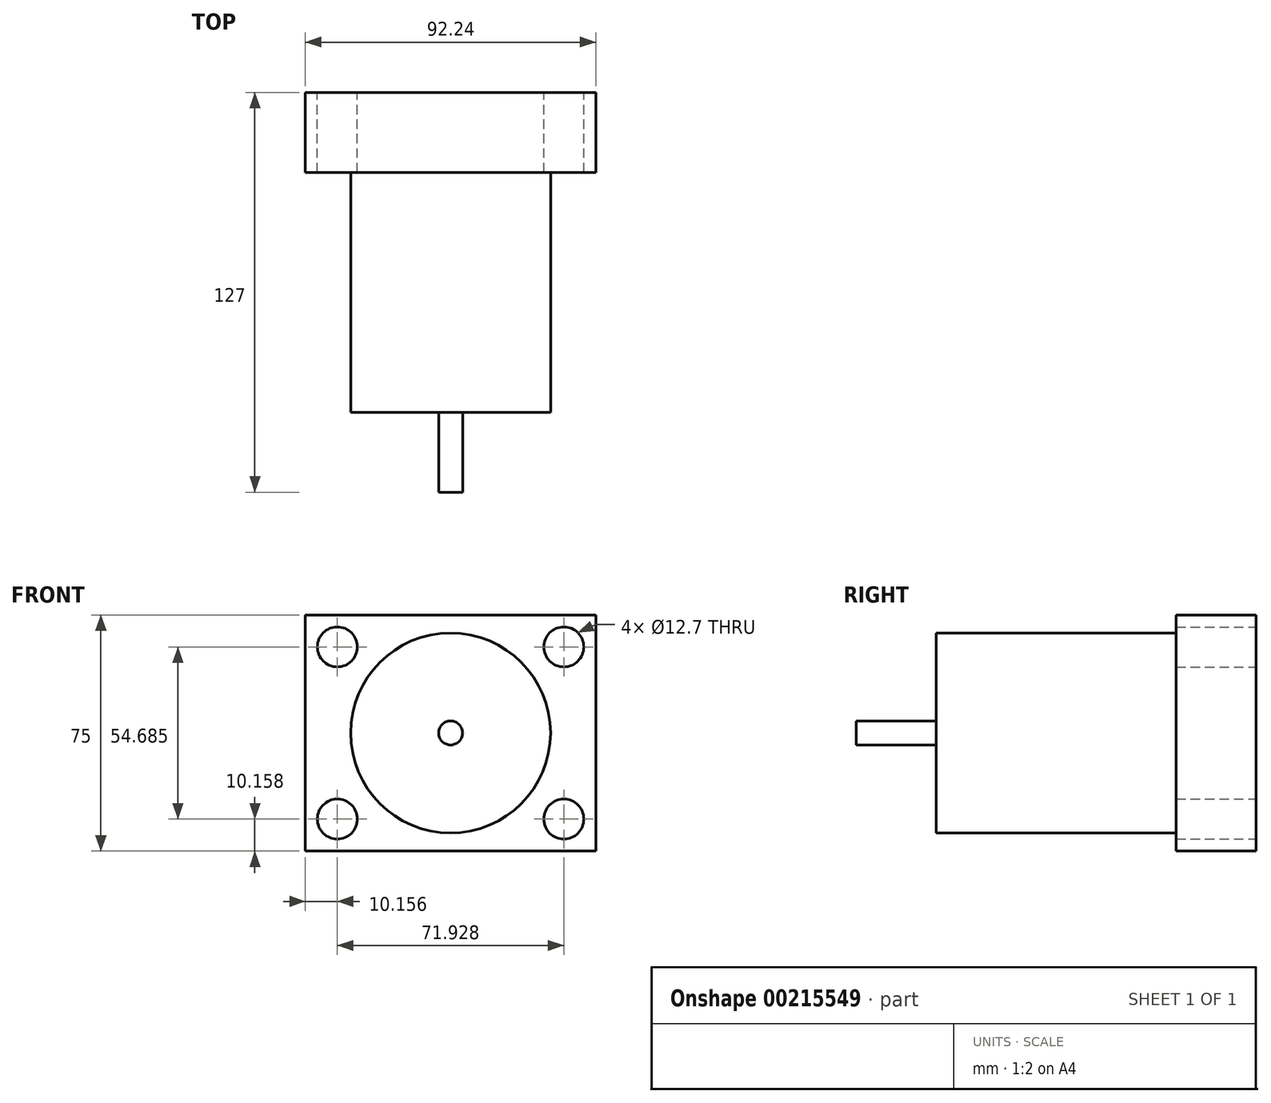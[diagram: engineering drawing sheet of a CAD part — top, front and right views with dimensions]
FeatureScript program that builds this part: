
annotation { "Feature Type Name" : "Feature", "Feature Type Description" : "" }
export const myFeature = defineFeature(function(context is Context, id is Id, definition is map)
    precondition{}
    {
        {
            var Q0;
            Q0=qCreatedBy(makeId("Front.planeOp"),FACE);
            var sketch = newSketch(context, id + "F0", { "sketchPlane" : qUnion([Q0])});
            skLineSegment(sketch, "E0.bottom", {"start": v(-46.12, 37.5) * mm, "end": v(46.12, 37.5) * mm});
            skLineSegment(sketch, "E0.top", {"start": v(-46.12, -37.5) * mm, "end": v(46.12, -37.5) * mm});
            skLineSegment(sketch, "E0.left", {"start": v(-46.12, 37.5) * mm, "end": v(-46.12, -37.5) * mm});
            skLineSegment(sketch, "E0.right", {"start": v(46.12, 37.5) * mm, "end": v(46.12, -37.5) * mm});
            skLineSegment(sketch, "E1", {"start": v(0, 37.5) * mm, "end": v(0, 0) * mm, "construction": true});
            skLineSegment(sketch, "E2", {"start": v(0, 0) * mm, "end": v(46.12, 0) * mm, "construction": true});
            skCircle(sketch, "E3", {"center": v(-35.96, 27.34) * mm, "radius": 6.35 * mm});
            skCircle(sketch, "E4", {"center": v(35.96, 27.34) * mm, "radius": 6.35 * mm});
            skCircle(sketch, "E5", {"center": v(-35.96, -27.34) * mm, "radius": 6.35 * mm});
            skCircle(sketch, "E6", {"center": v(35.96, -27.34) * mm, "radius": 6.35 * mm});
            skSolve(sketch);
        }
        {
            var Q0;
            Q0 = qSketchRegion(id + "F0", true);
            extrude(context, id + "F1", {"entities" : qUnion([Q0]), "depth" : 25.4 * mm});
        }
        {
            var Q0;
            Q0=makeQuery(id+"F1.opExtrude","CAP_FACE",FACE,{"disambiguationData":[OSD([sQuery(id+"F0.wireOp",EDGE,"E0.bottom"),sQuery(id+"F0.wireOp",EDGE,"E0.top"),sQuery(id+"F0.wireOp",EDGE,"E0.left"),sQuery(id+"F0.wireOp",EDGE,"E0.right"),sQuery(id+"F0.wireOp",EDGE,"E3"),sQuery(id+"F0.wireOp",EDGE,"E4"),sQuery(id+"F0.wireOp",EDGE,"E5"),sQuery(id+"F0.wireOp",EDGE,"E6")])],"isStart":false});
            var sketch = newSketch(context, id + "F2", { "sketchPlane" : qUnion([Q0])});
            skCircle(sketch, "E7", {"center": v(0, 0) * mm, "radius": 31.75 * mm});
            skSolve(sketch);
        }
        {
            var Q0;
            Q0 = qSketchRegion(id + "F2", true);
            extrude(context, id + "F3", {"entities" : qUnion([Q0]), "operationType" : NewBodyOperationType.ADD, "depth" : 76.2 * mm});
        }
        {
            var Q0;
            Q0=makeQuery(id+"F3.opExtrude","CAP_FACE",FACE,{"disambiguationData":[OSD([sQuery(id+"F2.wireOp",EDGE,"E7")])],"isStart":false});
            var sketch = newSketch(context, id + "F4", { "sketchPlane" : qUnion([Q0])});
            skCircle(sketch, "E8", {"center": v(0, 0) * mm, "radius": 3.81 * mm});
            skSolve(sketch);
        }
        {
            var Q0;
            Q0 = qSketchRegion(id + "F4", true);
            extrude(context, id + "F5", {"entities" : qUnion([Q0]), "operationType" : NewBodyOperationType.ADD, "depth" : 25.4 * mm});
        }
    });
